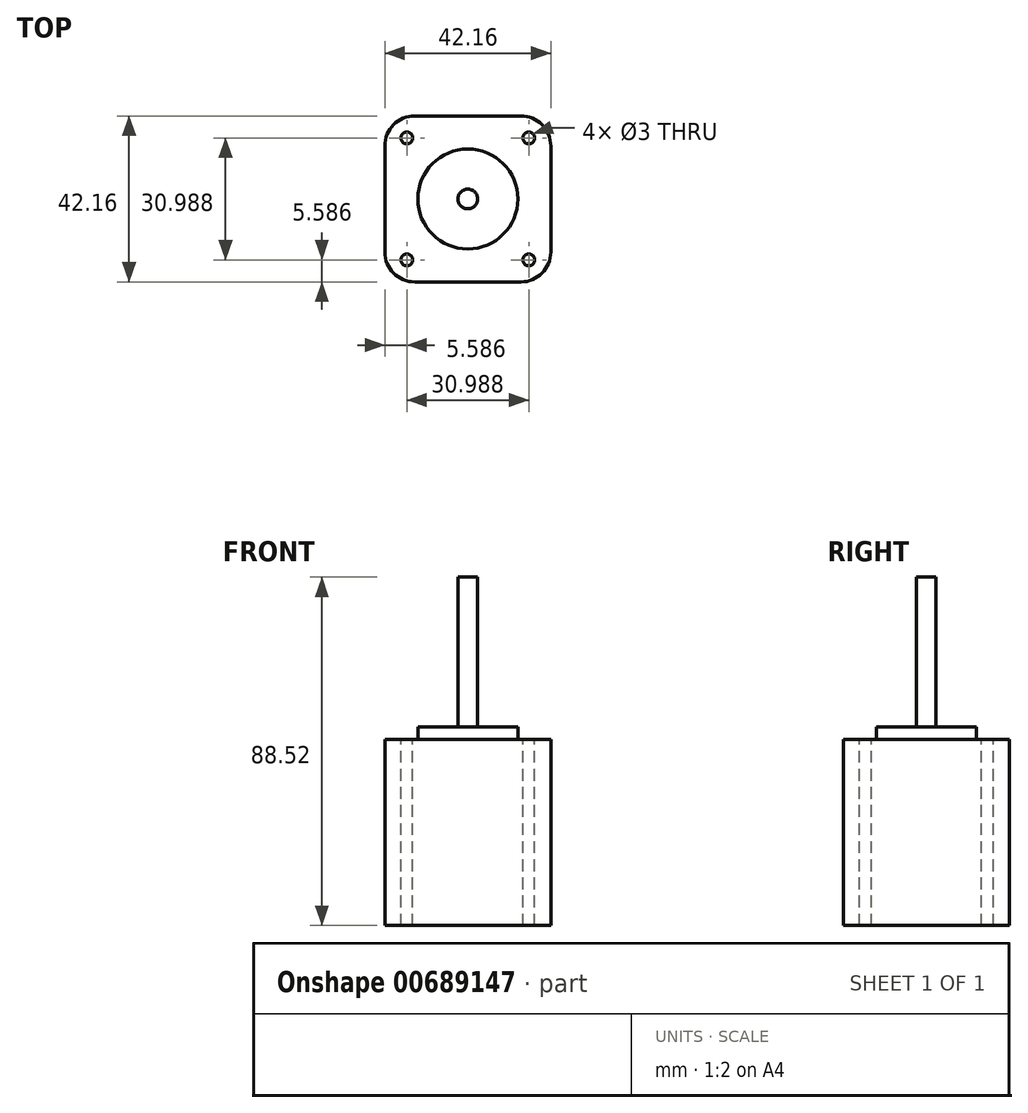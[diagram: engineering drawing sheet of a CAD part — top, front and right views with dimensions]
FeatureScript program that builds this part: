
annotation { "Feature Type Name" : "Feature", "Feature Type Description" : "" }
export const myFeature = defineFeature(function(context is Context, id is Id, definition is map)
    precondition{}
    {
        {
            var Q0;
            Q0=qCreatedBy(makeId("Top.planeOp"),FACE);
            var sketch = newSketch(context, id + "F0", { "sketchPlane" : qUnion([Q0])});
            skLineSegment(sketch, "E0.bottom", {"start": v(21.08, 21.08) * mm, "end": v(-21.08, 21.08) * mm});
            skLineSegment(sketch, "E0.top", {"start": v(21.08, -21.08) * mm, "end": v(-21.08, -21.08) * mm});
            skLineSegment(sketch, "E0.left", {"start": v(21.08, 21.08) * mm, "end": v(21.08, -21.08) * mm});
            skLineSegment(sketch, "E0.right", {"start": v(-21.08, 21.08) * mm, "end": v(-21.08, -21.08) * mm});
            skPoint(sketch, "E0.middle", {"position": v(0, 0) * mm});
            skSolve(sketch);
        }
        {
            var Q0;
            Q0=makeQuery(id+"F0.imprint","IMPRINT",FACE,{"disambiguationData":[TD([[makeQuery(id+"F0.imprint","IMPRINT",EDGE,{"derivedFrom":sQuery(id+"F0.wireOp",EDGE,"E0.bottom")}),1.0]])]});
            extrude(context, id + "F1", {"entities" : qUnion([Q0]), "oppositeDirection" : true, "depth" : 47.24 * mm, "offsetDistance" : 25.4 * mm});
        }
        {
            var Q0;
            Q0=makeQuery(id+"F1.opExtrude","SWEPT_EDGE",EDGE,{"disambiguationData":[OSD([sQuery(id+"F0.wireOp",EDGE,"E0.top"),sQuery(id+"F0.wireOp",EDGE,"E0.left")])]});
            var Q1;
            Q1=makeQuery(id+"F1.opExtrude","SWEPT_EDGE",EDGE,{"disambiguationData":[OSD([sQuery(id+"F0.wireOp",EDGE,"E0.bottom"),sQuery(id+"F0.wireOp",EDGE,"E0.left")])]});
            var Q2;
            Q2=makeQuery(id+"F1.opExtrude","SWEPT_EDGE",EDGE,{"disambiguationData":[OSD([sQuery(id+"F0.wireOp",EDGE,"E0.bottom"),sQuery(id+"F0.wireOp",EDGE,"E0.right")])]});
            var Q3;
            Q3=makeQuery(id+"F1.opExtrude","SWEPT_EDGE",EDGE,{"disambiguationData":[OSD([sQuery(id+"F0.wireOp",EDGE,"E0.top"),sQuery(id+"F0.wireOp",EDGE,"E0.right")])]});
            fillet(context, id + "F2", {"entities" : qUnion([Q0, Q1, Q2, Q3]), "radius" : 7.62 * mm, "tangentPropagation" : true, "allowEdgeOverflow" : false});
        }
        {
            var Q0;
            Q0=makeQuery(id+"F1.opExtrude","CAP_FACE",FACE,{"disambiguationData":[OSD([sQuery(id+"F0.wireOp",EDGE,"E0.bottom"),sQuery(id+"F0.wireOp",EDGE,"E0.top"),sQuery(id+"F0.wireOp",EDGE,"E0.left"),sQuery(id+"F0.wireOp",EDGE,"E0.right")])],"isStart":true});
            var sketch = newSketch(context, id + "F3", { "sketchPlane" : qUnion([Q0])});
            skCircle(sketch, "E1", {"center": v(0, 0) * mm, "radius": 12.7 * mm});
            skSolve(sketch);
        }
        {
            var Q0;
            Q0=makeQuery(id+"F3.imprint","IMPRINT",FACE,{"disambiguationData":[TD([[makeQuery(id+"F3.imprint","IMPRINT",EDGE,{"derivedFrom":sQuery(id+"F3.wireOp",EDGE,"E1")}),1.0]])]});
            extrude(context, id + "F4", {"entities" : qUnion([Q0]), "operationType" : NewBodyOperationType.ADD, "depth" : 3.17 * mm, "offsetDistance" : 25.4 * mm});
        }
        {
            var Q0;
            Q0=makeQuery(id+"F4.opExtrude","CAP_FACE",FACE,{"disambiguationData":[OSD([sQuery(id+"F3.wireOp",EDGE,"E1")])],"isStart":false});
            var sketch = newSketch(context, id + "F5", { "sketchPlane" : qUnion([Q0])});
            skCircle(sketch, "E2", {"center": v(0, 0) * mm, "radius": 2.5 * mm});
            skSolve(sketch);
        }
        {
            var Q0;
            Q0=makeQuery(id+"F5.imprint","IMPRINT",FACE,{"disambiguationData":[TD([[makeQuery(id+"F5.imprint","IMPRINT",EDGE,{"derivedFrom":sQuery(id+"F5.wireOp",EDGE,"E2")}),1.0]])]});
            extrude(context, id + "F6", {"entities" : qUnion([Q0]), "operationType" : NewBodyOperationType.ADD, "depth" : 38.1 * mm, "offsetDistance" : 25.4 * mm});
        }
        {
            var Q0;
            Q0=makeQuery(id+"F1.opExtrude","CAP_FACE",FACE,{"disambiguationData":[OSD([sQuery(id+"F0.wireOp",EDGE,"E0.bottom"),sQuery(id+"F0.wireOp",EDGE,"E0.top"),sQuery(id+"F0.wireOp",EDGE,"E0.left"),sQuery(id+"F0.wireOp",EDGE,"E0.right")])],"isStart":true});
            var sketch = newSketch(context, id + "F7", { "sketchPlane" : qUnion([Q0])});
            skLineSegment(sketch, "E3.bottom", {"start": v(15.5, 15.5) * mm, "end": v(-15.5, 15.5) * mm});
            skLineSegment(sketch, "E3.top", {"start": v(15.5, -15.5) * mm, "end": v(-15.5, -15.5) * mm});
            skLineSegment(sketch, "E3.left", {"start": v(15.5, 15.5) * mm, "end": v(15.5, -15.5) * mm});
            skLineSegment(sketch, "E3.right", {"start": v(-15.5, 15.5) * mm, "end": v(-15.5, -15.5) * mm});
            skPoint(sketch, "E3.middle", {"position": v(0, 0) * mm});
            skCircle(sketch, "E4", {"center": v(-15.5, 15.5) * mm, "radius": 1.5 * mm});
            skCircle(sketch, "E5", {"center": v(15.5, 15.5) * mm, "radius": 1.5 * mm});
            skCircle(sketch, "E6", {"center": v(15.5, -15.5) * mm, "radius": 1.5 * mm});
            skCircle(sketch, "E7", {"center": v(-15.5, -15.5) * mm, "radius": 1.5 * mm});
            skSolve(sketch);
        }
        {
            var Q0;
            {var subQ0=sQuery(id+"F7.wireOp",EDGE,"E3.right");var subQ1=sQuery(id+"F7.wireOp",EDGE,"E3.bottom");var subQ2=makeQuery(id+"F7.imprint","INTERSECT",VERTEX,{"derivedFrom":[subQ1,subQ0]});Q0=makeQuery(id+"F7.imprint","IMPRINT",FACE,{"disambiguationData":[TD([[makeQuery(id+"F7.imprint","IMPRINT",EDGE,{"disambiguationData":[TD([[subQ2,1.0]])],"derivedFrom":subQ1}),-1.0]])]});}
            var Q1;
            {var subQ0=sQuery(id+"F7.wireOp",EDGE,"E3.right");var subQ1=sQuery(id+"F7.wireOp",EDGE,"E3.bottom");var subQ2=makeQuery(id+"F7.imprint","INTERSECT",VERTEX,{"derivedFrom":[subQ1,subQ0]});Q1=makeQuery(id+"F7.imprint","IMPRINT",FACE,{"disambiguationData":[TD([[makeQuery(id+"F7.imprint","IMPRINT",EDGE,{"disambiguationData":[TD([[subQ2,1.0]])],"derivedFrom":subQ1}),1.0]])]});}
            var Q2;
            {var subQ0=sQuery(id+"F7.wireOp",EDGE,"E3.left");var subQ1=sQuery(id+"F7.wireOp",EDGE,"E3.bottom");var subQ2=makeQuery(id+"F7.imprint","INTERSECT",VERTEX,{"derivedFrom":[subQ1,subQ0]});Q2=makeQuery(id+"F7.imprint","IMPRINT",FACE,{"disambiguationData":[TD([[makeQuery(id+"F7.imprint","IMPRINT",EDGE,{"disambiguationData":[TD([[subQ2,-1.0]])],"derivedFrom":subQ1}),1.0]])]});}
            var Q3;
            {var subQ0=sQuery(id+"F7.wireOp",EDGE,"E3.left");var subQ1=sQuery(id+"F7.wireOp",EDGE,"E3.bottom");var subQ2=makeQuery(id+"F7.imprint","INTERSECT",VERTEX,{"derivedFrom":[subQ1,subQ0]});Q3=makeQuery(id+"F7.imprint","IMPRINT",FACE,{"disambiguationData":[TD([[makeQuery(id+"F7.imprint","IMPRINT",EDGE,{"disambiguationData":[TD([[subQ2,-1.0]])],"derivedFrom":subQ1}),-1.0]])]});}
            var Q4;
            {var subQ0=sQuery(id+"F7.wireOp",EDGE,"E3.left");var subQ1=sQuery(id+"F7.wireOp",EDGE,"E3.top");var subQ2=makeQuery(id+"F7.imprint","INTERSECT",VERTEX,{"derivedFrom":[subQ1,subQ0]});Q4=makeQuery(id+"F7.imprint","IMPRINT",FACE,{"disambiguationData":[TD([[makeQuery(id+"F7.imprint","IMPRINT",EDGE,{"disambiguationData":[TD([[subQ2,-1.0]])],"derivedFrom":subQ1}),1.0]])]});}
            var Q5;
            {var subQ0=sQuery(id+"F7.wireOp",EDGE,"E3.left");var subQ1=sQuery(id+"F7.wireOp",EDGE,"E3.top");var subQ2=makeQuery(id+"F7.imprint","INTERSECT",VERTEX,{"derivedFrom":[subQ1,subQ0]});Q5=makeQuery(id+"F7.imprint","IMPRINT",FACE,{"disambiguationData":[TD([[makeQuery(id+"F7.imprint","IMPRINT",EDGE,{"disambiguationData":[TD([[subQ2,-1.0]])],"derivedFrom":subQ1}),-1.0]])]});}
            var Q6;
            {var subQ0=sQuery(id+"F7.wireOp",EDGE,"E3.right");var subQ1=sQuery(id+"F7.wireOp",EDGE,"E3.top");var subQ2=makeQuery(id+"F7.imprint","INTERSECT",VERTEX,{"derivedFrom":[subQ1,subQ0]});Q6=makeQuery(id+"F7.imprint","IMPRINT",FACE,{"disambiguationData":[TD([[makeQuery(id+"F7.imprint","IMPRINT",EDGE,{"disambiguationData":[TD([[subQ2,1.0]])],"derivedFrom":subQ1}),1.0]])]});}
            var Q7;
            {var subQ0=sQuery(id+"F7.wireOp",EDGE,"E3.right");var subQ1=sQuery(id+"F7.wireOp",EDGE,"E3.top");var subQ2=makeQuery(id+"F7.imprint","INTERSECT",VERTEX,{"derivedFrom":[subQ1,subQ0]});Q7=makeQuery(id+"F7.imprint","IMPRINT",FACE,{"disambiguationData":[TD([[makeQuery(id+"F7.imprint","IMPRINT",EDGE,{"disambiguationData":[TD([[subQ2,1.0]])],"derivedFrom":subQ1}),-1.0]])]});}
            extrude(context, id + "F8", {"entities" : qUnion([Q0, Q1, Q2, Q3, Q4, Q5, Q6, Q7]), "operationType" : NewBodyOperationType.REMOVE, "endBound" : BoundingType.THROUGH_ALL, "oppositeDirection" : true, "depth" : 25.4 * mm, "offsetDistance" : 25.4 * mm});
        }
    });
